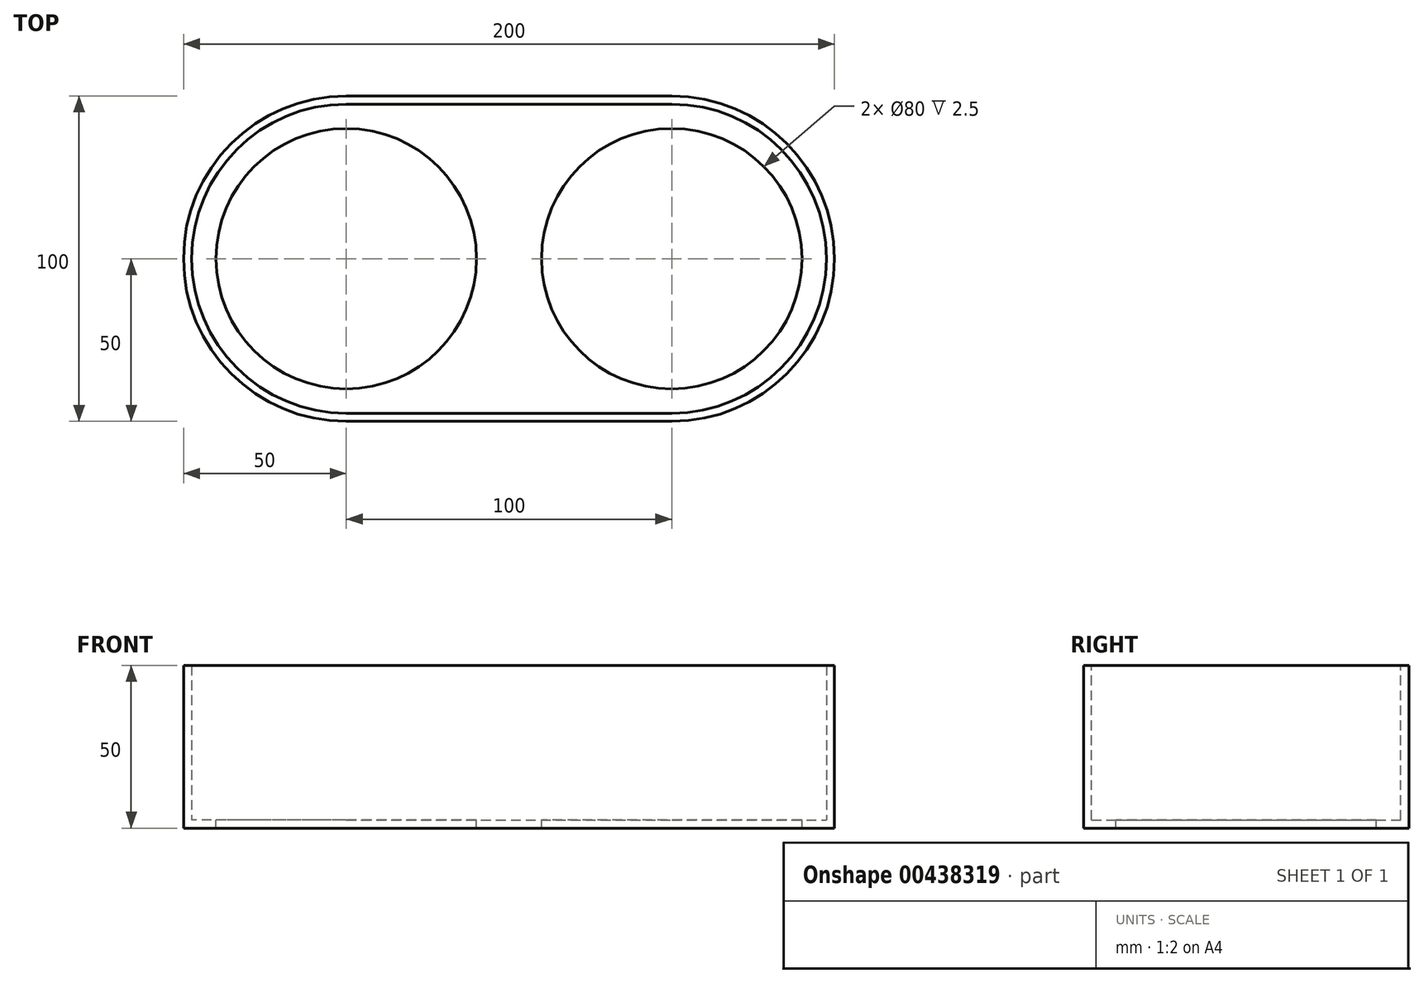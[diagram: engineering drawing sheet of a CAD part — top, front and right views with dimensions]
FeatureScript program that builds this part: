
annotation { "Feature Type Name" : "Feature", "Feature Type Description" : "" }
export const myFeature = defineFeature(function(context is Context, id is Id, definition is map)
    precondition{}
    {
        {
            var Q0;
            Q0=qCreatedBy(makeId("Top.planeOp"),FACE);
            var sketch = newSketch(context, id + "F0", { "sketchPlane" : qUnion([Q0])});
            skLineSegment(sketch, "E0.bottom", {"start": v(-50, 50) * mm, "end": v(50, 50) * mm});
            skLineSegment(sketch, "E0.top", {"start": v(-50, -50) * mm, "end": v(50, -50) * mm});
            skArc(sketch, "E1", {"start": v(50, -50) * mm, "mid": v(100, 0) * mm, "end": v(50, 50) * mm});
            skArc(sketch, "E2", {"start": v(-50, 50) * mm, "mid": v(-100, 0) * mm, "end": v(-50, -50) * mm});
            skSolve(sketch);
        }
        {
            var Q0;
            Q0 = qSketchRegion(id + "F0", true);
            extrude(context, id + "F1", {"entities" : qUnion([Q0]), "depth" : 50 * mm});
        }
        {
            var Q0;
            Q0=makeQuery(id+"F1.opExtrude","CAP_FACE",FACE,{"disambiguationData":[OSD([sQuery(id+"F0.wireOp",EDGE,"E0.bottom"),sQuery(id+"F0.wireOp",EDGE,"E0.top"),sQuery(id+"F0.wireOp",EDGE,"E1"),sQuery(id+"F0.wireOp",EDGE,"E2")])],"isStart":false});
            shell(context, id + "F2", {"entities" : qUnion([Q0]), "thickness" : 2.5 * mm});
        }
        {
            var Q0;
            Q0=makeQuery(id+"F2.opShell","OFFSET_FACE",FACE,{"disambiguationData":[OSD([sQuery(id+"F0.wireOp",EDGE,"E0.bottom"),sQuery(id+"F0.wireOp",EDGE,"E0.top"),sQuery(id+"F0.wireOp",EDGE,"E1"),sQuery(id+"F0.wireOp",EDGE,"E2")])]});
            var sketch = newSketch(context, id + "F3", { "sketchPlane" : qUnion([Q0])});
            skCircle(sketch, "E3", {"center": v(-50, 0) * mm, "radius": 40 * mm});
            skCircle(sketch, "E4", {"center": v(50, 0) * mm, "radius": 40 * mm});
            skSolve(sketch);
        }
        {
            var Q0;
            Q0 = qSketchRegion(id + "F3", true);
            extrude(context, id + "F4", {"entities" : qUnion([Q0]), "operationType" : NewBodyOperationType.REMOVE, "oppositeDirection" : true, "depth" : 25 * mm});
        }
    });
